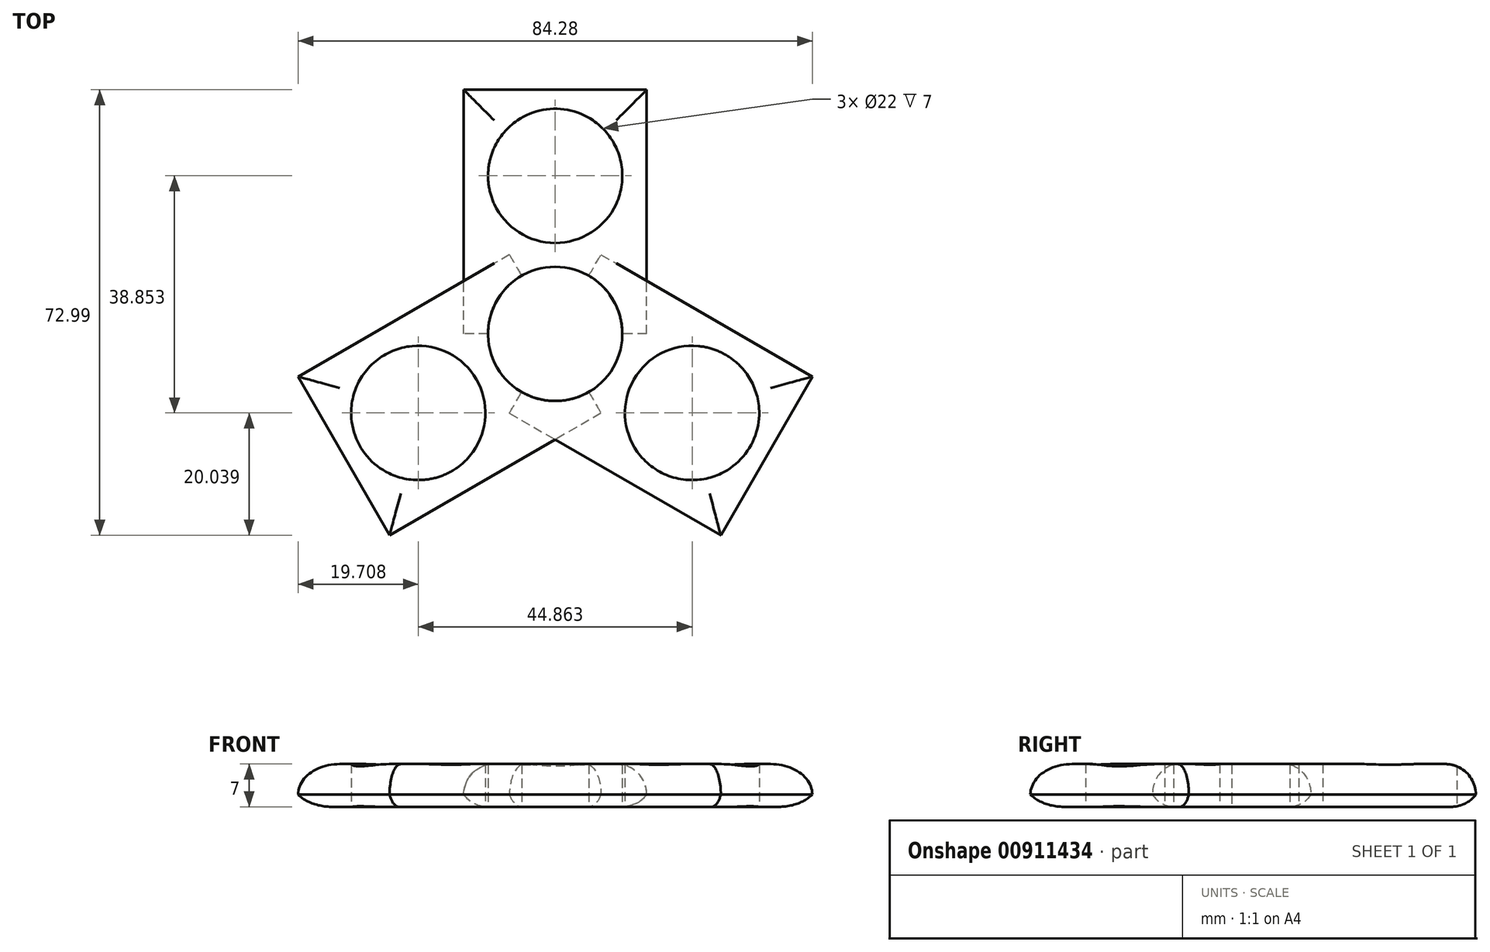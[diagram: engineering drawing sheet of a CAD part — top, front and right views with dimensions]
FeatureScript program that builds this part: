
annotation { "Feature Type Name" : "Feature", "Feature Type Description" : "" }
export const myFeature = defineFeature(function(context is Context, id is Id, definition is map)
    precondition{}
    {
        {
            var Q0;
            Q0=qCreatedBy(makeId("Top.planeOp"),FACE);
            var sketch = newSketch(context, id + "F0", { "sketchPlane" : qUnion([Q0])});
            skCircle(sketch, "E0", {"center": v(0, 0) * mm, "radius": 11 * mm});
            skLineSegment(sketch, "E1.bottom", {"start": v(0, 0) * mm, "end": v(15, 0) * mm});
            skLineSegment(sketch, "E1.top", {"start": v(0, 40) * mm, "end": v(15, 40) * mm});
            skLineSegment(sketch, "E1.left", {"start": v(0, 0) * mm, "end": v(0, 40) * mm});
            skLineSegment(sketch, "E1.right", {"start": v(15, 0) * mm, "end": v(15, 40) * mm});
            skLineSegment(sketch, "E2.bottom", {"start": v(0, 0) * mm, "end": v(-15, 0) * mm});
            skLineSegment(sketch, "E2.top", {"start": v(0, 40) * mm, "end": v(-15, 40) * mm});
            skLineSegment(sketch, "E2.right", {"start": v(-15, 0) * mm, "end": v(-15, 40) * mm});
            skLineSegment(sketch, "E3", {"start": v(0, 40) * mm, "end": v(0, 25.9) * mm});
            skCircle(sketch, "E4", {"center": v(0, 25.9) * mm, "radius": 11 * mm});
            skSolve(sketch);
        }
        {
            var Q0;
            {var subQ0=sQuery(id+"F0.wireOp",EDGE,"E2.top");Q0=makeQuery(id+"F0.imprint","IMPRINT",FACE,{"disambiguationData":[TD([[makeQuery(id+"F0.imprint","IMPRINT",EDGE,{"derivedFrom":subQ0}),1.0]])]});}
            var Q1;
            {var subQ9=sQuery(id+"F0.wireOp",EDGE,"E1.top");Q1=makeQuery(id+"F0.imprint","IMPRINT",FACE,{"disambiguationData":[TD([[makeQuery(id+"F0.imprint","IMPRINT",EDGE,{"derivedFrom":subQ9}),-1.0]])]});}
            extrude(context, id + "F1", {"entities" : qUnion([Q0, Q1]), "depth" : 7 * mm, "offsetDistance" : 25 * mm});
        }
        {
            var Q0;
            Q0=qCreatedBy(makeId("Front.planeOp"),FACE);
            var sketch = newSketch(context, id + "F2", { "sketchPlane" : qUnion([Q0])});
            skLineSegment(sketch, "E5", {"start": v(0, 0) * mm, "end": v(0, 54.89) * mm});
            skSolve(sketch);
        }
        {
            var Q0;
            Q0=makeQuery(id+"F1.opExtrude","SWEPT_BODY",BODY,{"disambiguationData":[OSD([sQuery(id+"F0.wireOp",EDGE,"E0"),sQuery(id+"F0.wireOp",EDGE,"E1.bottom"),sQuery(id+"F0.wireOp",EDGE,"E1.top"),sQuery(id+"F0.wireOp",EDGE,"E1.right"),sQuery(id+"F0.wireOp",EDGE,"E2.bottom"),sQuery(id+"F0.wireOp",EDGE,"E2.top"),sQuery(id+"F0.wireOp",EDGE,"E2.right"),sQuery(id+"F0.wireOp",EDGE,"E4")])]});
            var Q1;
            Q1=sQuery(id+"F2.wireOp",EDGE,"E5");
            transform(context, id + "F3", {"entities" : qUnion([Q0]), "transformType" : TransformType.ROTATION, "transformAxis" : qUnion([Q1]), "angle" : 120 * degree, "makeCopy" : true});
        }
        {
            var Q0;
            Q0=makeQuery(id+"F1.opExtrude","SWEPT_BODY",BODY,{"disambiguationData":[OSD([sQuery(id+"F0.wireOp",EDGE,"E0"),sQuery(id+"F0.wireOp",EDGE,"E1.bottom"),sQuery(id+"F0.wireOp",EDGE,"E1.top"),sQuery(id+"F0.wireOp",EDGE,"E1.right"),sQuery(id+"F0.wireOp",EDGE,"E2.bottom"),sQuery(id+"F0.wireOp",EDGE,"E2.top"),sQuery(id+"F0.wireOp",EDGE,"E2.right"),sQuery(id+"F0.wireOp",EDGE,"E4")])]});
            var Q1;
            Q1=sQuery(id+"F2.wireOp",EDGE,"E5");
            transform(context, id + "F4", {"entities" : qUnion([Q0]), "transformType" : TransformType.ROTATION, "transformAxis" : qUnion([Q1]), "angle" : 240 * degree, "makeCopy" : true});
        }
        {
            var Q0;
            Q0=makeQuery(id+"F1.opExtrude","CAP_EDGE",EDGE,{"disambiguationData":[OSD([sQuery(id+"F0.wireOp",EDGE,"E1.top"),sQuery(id+"F0.wireOp",EDGE,"E2.top")])],"isStart":false});
            var Q1;
            Q1=makeQuery(id+"F1.opExtrude","CAP_EDGE",EDGE,{"disambiguationData":[OSD([sQuery(id+"F0.wireOp",EDGE,"E2.right")])],"isStart":false});
            var Q2;
            Q2=makeQuery(id+"F1.opExtrude","CAP_EDGE",EDGE,{"disambiguationData":[OSD([sQuery(id+"F0.wireOp",EDGE,"E1.right")])],"isStart":false});
            var Q3;
            Q3=makeQuery(id+"F4.opPattern","COPY",EDGE,{"derivedFrom":makeQuery(id+"F1.opExtrude","CAP_EDGE",EDGE,{"disambiguationData":[OSD([sQuery(id+"F0.wireOp",EDGE,"E2.right")])],"isStart":false}),"instanceName":"1"});
            var Q4;
            Q4=makeQuery(id+"F4.opPattern","COPY",EDGE,{"derivedFrom":makeQuery(id+"F1.opExtrude","CAP_EDGE",EDGE,{"disambiguationData":[OSD([sQuery(id+"F0.wireOp",EDGE,"E1.top"),sQuery(id+"F0.wireOp",EDGE,"E2.top")])],"isStart":false}),"instanceName":"1"});
            var Q5;
            Q5=makeQuery(id+"F4.opPattern","COPY",EDGE,{"derivedFrom":makeQuery(id+"F1.opExtrude","CAP_EDGE",EDGE,{"disambiguationData":[OSD([sQuery(id+"F0.wireOp",EDGE,"E1.right")])],"isStart":false}),"instanceName":"1"});
            var Q6;
            Q6=makeQuery(id+"F3.opPattern","COPY",EDGE,{"derivedFrom":makeQuery(id+"F1.opExtrude","CAP_EDGE",EDGE,{"disambiguationData":[OSD([sQuery(id+"F0.wireOp",EDGE,"E2.right")])],"isStart":false}),"instanceName":"1"});
            var Q7;
            Q7=makeQuery(id+"F3.opPattern","COPY",EDGE,{"derivedFrom":makeQuery(id+"F1.opExtrude","CAP_EDGE",EDGE,{"disambiguationData":[OSD([sQuery(id+"F0.wireOp",EDGE,"E1.top"),sQuery(id+"F0.wireOp",EDGE,"E2.top")])],"isStart":false}),"instanceName":"1"});
            var Q8;
            Q8=makeQuery(id+"F3.opPattern","COPY",EDGE,{"derivedFrom":makeQuery(id+"F1.opExtrude","CAP_EDGE",EDGE,{"disambiguationData":[OSD([sQuery(id+"F0.wireOp",EDGE,"E1.right")])],"isStart":false}),"instanceName":"1"});
            fillet(context, id + "F5", {"entities" : qUnion([Q0, Q1, Q2, Q3, Q4, Q5, Q6, Q7, Q8]), "radius" : 5 * mm, "tangentPropagation" : true, "allowEdgeOverflow" : false});
        }
        {
            var Q0;
            Q0=makeQuery(id+"F4.opPattern","COPY",EDGE,{"derivedFrom":makeQuery(id+"F1.opExtrude","CAP_EDGE",EDGE,{"disambiguationData":[OSD([sQuery(id+"F0.wireOp",EDGE,"E2.right")])],"isStart":true}),"instanceName":"1"});
            var Q1;
            Q1=makeQuery(id+"F1.opExtrude","CAP_EDGE",EDGE,{"disambiguationData":[OSD([sQuery(id+"F0.wireOp",EDGE,"E1.right")])],"isStart":true});
            var Q2;
            Q2=makeQuery(id+"F1.opExtrude","CAP_EDGE",EDGE,{"disambiguationData":[OSD([sQuery(id+"F0.wireOp",EDGE,"E1.top"),sQuery(id+"F0.wireOp",EDGE,"E2.top")])],"isStart":true});
            var Q3;
            Q3=makeQuery(id+"F1.opExtrude","CAP_EDGE",EDGE,{"disambiguationData":[OSD([sQuery(id+"F0.wireOp",EDGE,"E2.right")])],"isStart":true});
            var Q4;
            Q4=makeQuery(id+"F3.opPattern","COPY",EDGE,{"derivedFrom":makeQuery(id+"F1.opExtrude","CAP_EDGE",EDGE,{"disambiguationData":[OSD([sQuery(id+"F0.wireOp",EDGE,"E1.right")])],"isStart":true}),"instanceName":"1"});
            var Q5;
            Q5=makeQuery(id+"F3.opPattern","COPY",EDGE,{"derivedFrom":makeQuery(id+"F1.opExtrude","CAP_EDGE",EDGE,{"disambiguationData":[OSD([sQuery(id+"F0.wireOp",EDGE,"E1.top"),sQuery(id+"F0.wireOp",EDGE,"E2.top")])],"isStart":true}),"instanceName":"1"});
            var Q6;
            Q6=makeQuery(id+"F3.opPattern","COPY",EDGE,{"derivedFrom":makeQuery(id+"F1.opExtrude","CAP_EDGE",EDGE,{"disambiguationData":[OSD([sQuery(id+"F0.wireOp",EDGE,"E2.right")])],"isStart":true}),"instanceName":"1"});
            var Q7;
            Q7=makeQuery(id+"F4.opPattern","COPY",EDGE,{"derivedFrom":makeQuery(id+"F1.opExtrude","CAP_EDGE",EDGE,{"disambiguationData":[OSD([sQuery(id+"F0.wireOp",EDGE,"E1.right")])],"isStart":true}),"instanceName":"1"});
            var Q8;
            Q8=makeQuery(id+"F4.opPattern","COPY",EDGE,{"derivedFrom":makeQuery(id+"F1.opExtrude","CAP_EDGE",EDGE,{"disambiguationData":[OSD([sQuery(id+"F0.wireOp",EDGE,"E1.top"),sQuery(id+"F0.wireOp",EDGE,"E2.top")])],"isStart":true}),"instanceName":"1"});
            fillet(context, id + "F6", {"entities" : qUnion([Q0, Q1, Q2, Q3, Q4, Q5, Q6, Q7, Q8]), "radius" : 5 * mm, "tangentPropagation" : true, "allowEdgeOverflow" : false});
        }
    });
